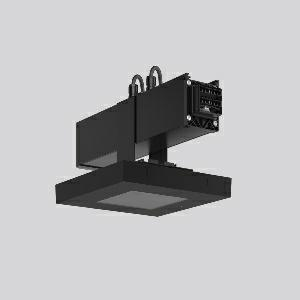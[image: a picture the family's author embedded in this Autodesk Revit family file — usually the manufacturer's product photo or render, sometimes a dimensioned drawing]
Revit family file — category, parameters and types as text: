
# Revit family: linedo_module_rw_9503rw_763_409_100_2470
name_source: partatom
category: Lighting Fixtures
units: mm (PartAtom-declared; Revit-internal decimal feet)

## family parameters
Cut with Voids When Loaded = No
Host = Face
Light Source = No
Part Type = Normal
Room Calculation Point = No
Round Connector Dimension = Use Diameter
Shared = No

## types (1)
- LINEDO Module RW (1 x LED Modul 765, 190 lm, 6500)
    Apparent Load = 4 VA
    CIE Flux Codes = 39 73 100 100 100
    Color Rendering = 70
    Color Temperature = 6500
    Default Elevation = 1800 mm
    Description = LINEDO, 4,2 W, 190 lm, 765, black, on/off
Continuous line luminaire, L 330 B 198 H 170, CBS, emergency-190 lm, AC-Control
    Height = 170 mm  [stored 0.557743 ft]
    Lamp = 1 x LED Modul 765
    Lamp Light Flux = 190 lm
    Lamp count = 1
    Length = 330 mm
    Lifetime = 50000 h
    Luminous efficacy = 45 lm/W
    Manufacturer = RZB
    ModVariant = No
    Model = 9503RW.763.409.100
    Mounting Place = Ceiling
    Mounting Type = Pendant, Surface mounted
    Number of Poles = 1
    OnlyDefault = Yes
    Power Factor = 1
    Product Name = LINEDO Module RW
    Product group = Surface mounted continuous line luminaire system
    ProductGroupID = 310
    Protection Class = Protection class I
    Protection Degree = IP 54
    RLX_Detail_Level = 1
    RLX_Emergency_Light_Flux = 190 lm
    RLX_Emergency_Type = 3
    RLX_Emergency_Type_DB = Yes
    RlxData = <blob elided: 34369 chars, md5=9688ad56>
    Socket = socket
    Standby Power = 0 W
    System Light Flux = 190 lm
    System Power = 4 W
    Type Comments = Product without accessories
    Type Image = 9503rw.763.434.000.jpg
    URL = http://relux.com
    VarID = ---
    Voltage = 230 V
    Voltage Range = 220-240 V
    Weight = 0.00 kg
    Width = 198 mm

note: [stored X ft] marks values corroborated as IEEE doubles in the binary element streams (Revit-internal decimal feet)

## geometry (parser evidence)
native form markers: Blend x4, Sweep x13
no freeform markers — native parametric forms only
